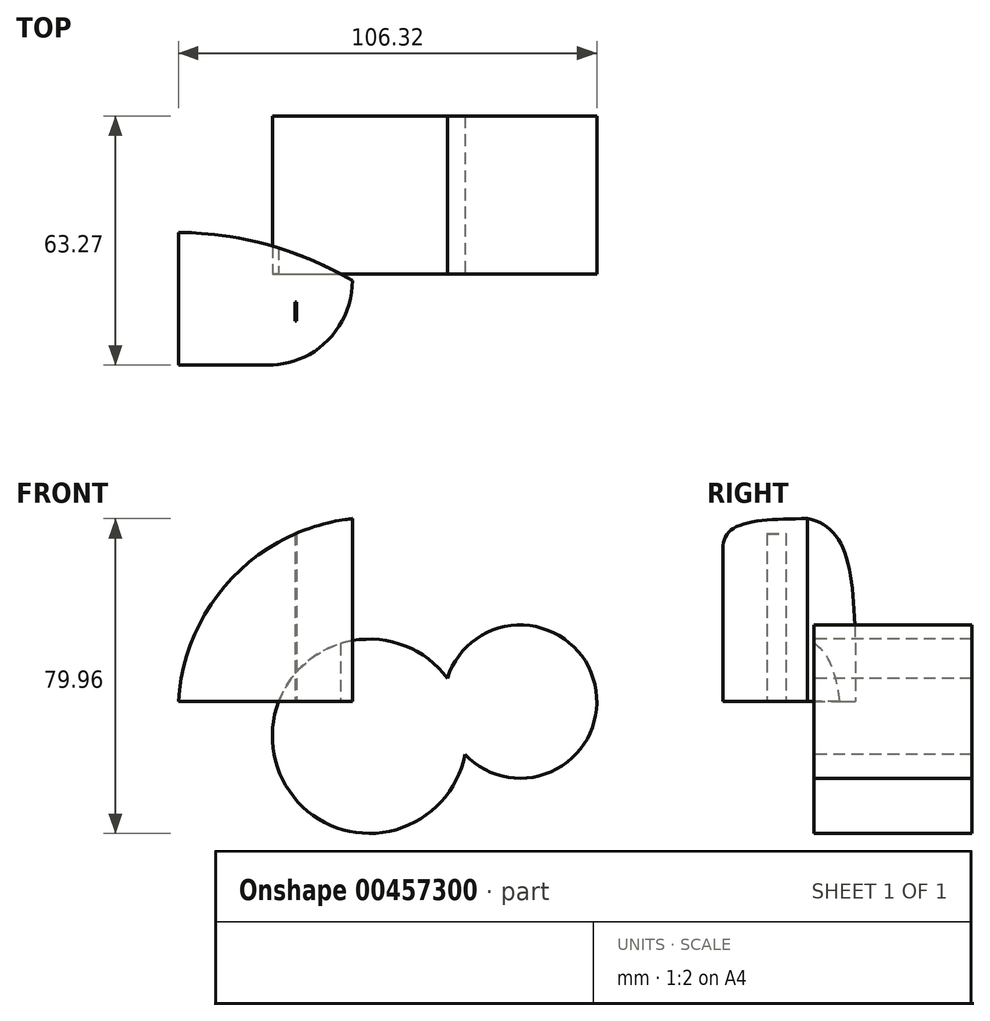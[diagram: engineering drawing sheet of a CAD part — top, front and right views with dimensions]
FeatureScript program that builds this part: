
annotation { "Feature Type Name" : "Feature", "Feature Type Description" : "" }
export const myFeature = defineFeature(function(context is Context, id is Id, definition is map)
    precondition{}
    {
        {
            var Q0;
            Q0=qCreatedBy(makeId("Top.planeOp"),FACE);
            var sketch = newSketch(context, id + "F0", { "sketchPlane" : qUnion([Q0])});
            skLineSegment(sketch, "E0.bottom", {"start": v(-21.82, 10.58) * mm, "end": v(22.48, 10.58) * mm});
            skLineSegment(sketch, "E0.top", {"start": v(-21.82, -23.14) * mm, "end": v(22.48, -23.14) * mm});
            skLineSegment(sketch, "E0.left", {"start": v(-21.82, 10.58) * mm, "end": v(-21.82, -23.14) * mm});
            skLineSegment(sketch, "E0.right", {"start": v(22.48, 10.58) * mm, "end": v(22.48, -23.14) * mm});
            skLineSegment(sketch, "E1.bottom", {"start": v(8.24, -11.87) * mm, "end": v(7.96, -11.87) * mm});
            skLineSegment(sketch, "E1.top", {"start": v(8.24, -7.15) * mm, "end": v(7.96, -7.15) * mm});
            skLineSegment(sketch, "E1.left", {"start": v(8.24, -11.87) * mm, "end": v(8.24, -7.15) * mm});
            skLineSegment(sketch, "E1.right", {"start": v(7.96, -11.87) * mm, "end": v(7.96, -7.15) * mm});
            skSolve(sketch);
        }
        {
            var Q0;
            Q0=makeQuery(id+"F0.imprint","IMPRINT",FACE,{"disambiguationData":[TD([[makeQuery(id+"F0.imprint","IMPRINT",EDGE,{"derivedFrom":sQuery(id+"F0.wireOp",EDGE,"E0.bottom")}),-1.0]])]});
            extrude(context, id + "F1", {"entities" : qUnion([Q0]), "depth" : 46.48 * mm});
        }
        {
            var Q0;
            Q0=makeQuery(id+"F1.opExtrude","CAP_EDGE",EDGE,{"disambiguationData":[OSD([sQuery(id+"F0.wireOp",EDGE,"E0.left")])],"isStart":false});
            fillet(context, id + "F2", {"entities" : qUnion([Q0]), "radius" : 49.67 * mm, "tangentPropagation" : true, "allowEdgeOverflow" : false});
        }
        {
            var Q0;
            Q0=makeQuery(id+"F1.opExtrude","SWEPT_EDGE",EDGE,{"disambiguationData":[OSD([sQuery(id+"F0.wireOp",EDGE,"E0.top"),sQuery(id+"F0.wireOp",EDGE,"E0.right")])]});
            fillet(context, id + "F3", {"entities" : qUnion([Q0]), "radius" : 21.46 * mm, "tangentPropagation" : true, "allowEdgeOverflow" : false});
        }
        {
            var Q0;
            Q0=makeQuery(id+"F1.opExtrude","SWEPT_EDGE",EDGE,{"disambiguationData":[OSD([sQuery(id+"F0.wireOp",EDGE,"E0.bottom"),sQuery(id+"F0.wireOp",EDGE,"E0.right")])]});
            var Q1;
            {var subQ0=sQuery(id+"F0.wireOp",EDGE,"E0.right");Q1=makeQuery(id+"F3.opFillet","BLEND_EDGE",EDGE,{"blendedFrom":[makeQuery(id+"F1.opExtrude","SWEPT_EDGE",EDGE,{"disambiguationData":[OSD([sQuery(id+"F0.wireOp",EDGE,"E0.top"),subQ0])]}),makeQuery(id+"F1.opExtrude","SWEPT_FACE",FACE,{"disambiguationData":[OSD([subQ0])]})],"blendedInto":[makeQuery(id+"F1.opExtrude","SWEPT_FACE",FACE,{"disambiguationData":[OSD([subQ0])]})]});}
            fillet(context, id + "F4", {"entities" : qUnion([Q0, Q1]), "radius" : 88.3 * mm, "tangentPropagation" : true, "allowEdgeOverflow" : false});
        }
        {
            var Q0;
            Q0=qCreatedBy(makeId("Front.planeOp"),FACE);
            var sketch = newSketch(context, id + "F5", { "sketchPlane" : qUnion([Q0])});
            skCircle(sketch, "E2", {"center": v(26.81, -8.8) * mm, "radius": 24.68 * mm});
            skCircle(sketch, "E3", {"center": v(65.12, 0) * mm, "radius": 19.46 * mm});
            skSolve(sketch);
        }
        {
            var Q0;
            Q0 = qSketchRegion(id + "F5", true);
            extrude(context, id + "F6", {"entities" : qUnion([Q0]), "operationType" : NewBodyOperationType.ADD, "oppositeDirection" : true, "depth" : 40.13 * mm});
        }
    });
